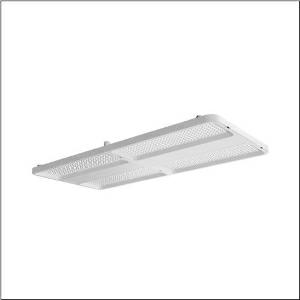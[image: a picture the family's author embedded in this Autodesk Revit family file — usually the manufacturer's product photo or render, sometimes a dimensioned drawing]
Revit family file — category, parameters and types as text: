
# Revit family: highbay_11_maxi_51hn11db4lda
name_source: partatom
category: Lighting Fixtures
units: mm (PartAtom-declared; Revit-internal decimal feet)

## family parameters
Cut with Voids When Loaded = No
Host = Face
Light Source = No
Part Type = Normal
Room Calculation Point = No
Round Connector Dimension = Use Diameter
Shared = No

## types (1)
- --- (1 x LED, 3960 lm, 19.5 W, 4000K)
    Apparent Load = 20 VA
    CIE Flux Codes = 85 97 100 100 100
    Color Rendering = 80
    Color Temperature = 4000K
    Default Elevation = 1800 mm
    Description = high bay luminaire Highbay 11 maxi; direct symmetric narrow distribution, light control with lens of PMMA; UGR ≤ 19 (X = 4H | Y = 8H | S = 0.25H | reflection values 70/50/20); luminous flux: 26.000lm; light colour: 840, colour temperature: 4000K, MacAdam ≤ 2 SDCM (initial), colour rendering: CRI > 80; luminous efficacy: 207,3lm/W; rated service life: 100.000h (L95/B50) at AT= 25°C; control: DALI 2; housing frame of high-performance plastic PA6, matt traffic white (RAL 9016); cover of PMMA; dimension (LxWxH): 946 x 442 x 72mm; luminaire connection: terminal, 5-pole, max. 2.5mm² (cable entry for one cable, Ø 8.5..16mm); mains connection: 230..240V, AC/DC 0/50..60Hz; connected load: 125,4W; protection rating (complete): IP66; insulation class (complete): insulation class I (protective earthing); protection symbol: D; impact resistance: IK08; halogen-free wiring; for central battery installations according to DIN EN 60598-2-22; corresponds to IFS (International Featured Standards) requirements for safety and quality in the food industry; LABS conformity tested according to VDMA 24364:2018-05; certification: CE, ENEC, VDE, UKCA; permissible operating ambient temperature: -40..+65°C (reducing of maximum allowable ambient temperature of 5°C with ceiling mounting); packaging unit: 1 piece; (delivery without accessories; please order mounting accessories separately)
    Height = 72 mm  [stored 0.23622 ft]
    Lamp = 1 x LED
    Lamp Light Flux = 3960 lm
    Lamp Power = 19.5 W
    Lamp count = 1
    Length = 946 mm
    Luminous efficacy = 203 lm/W
    Manufacturer = Siteco
    ModVariant = No
    Model = 51HN11DB4LDA
    Mounting Place = Ceiling
    Mounting Type = Pendant
    Number of Poles = 1
    OnlyDefault = Yes
    Power Factor = 1
    Product Name = Highbay 11 maxi
    Product group = high bay luminaire
    ProductGroupID = 901
    Protection Class = Protection class I
    Protection Degree = IP 66
    RLX_Detail_Level = 1
    RLX_Emergency_Light_Flux = 0 lm
    RLX_Emergency_Type = 0
    RLX_Emergency_Type_DB = No
    RlxData = <blob elided: 22201 chars, md5=631e2e71>
    Socket = socket
    Standby Power = 0 W
    System Light Flux = 3960 lm
    System Power = 20 W
    Type Comments = : DC mode (central or group accumulator) initial emergency light level
    Type Image = l_1363244.jpg
    URL = http://relux.com
    VarID = @adj_003707
    Voltage = 0 V
    Weight = 0.00 kg
    Width = 442 mm

note: [stored X ft] marks values corroborated as IEEE doubles in the binary element streams (Revit-internal decimal feet)

## geometry (parser evidence)
native form markers: Blend x4, Sweep x12
no freeform markers — native parametric forms only
